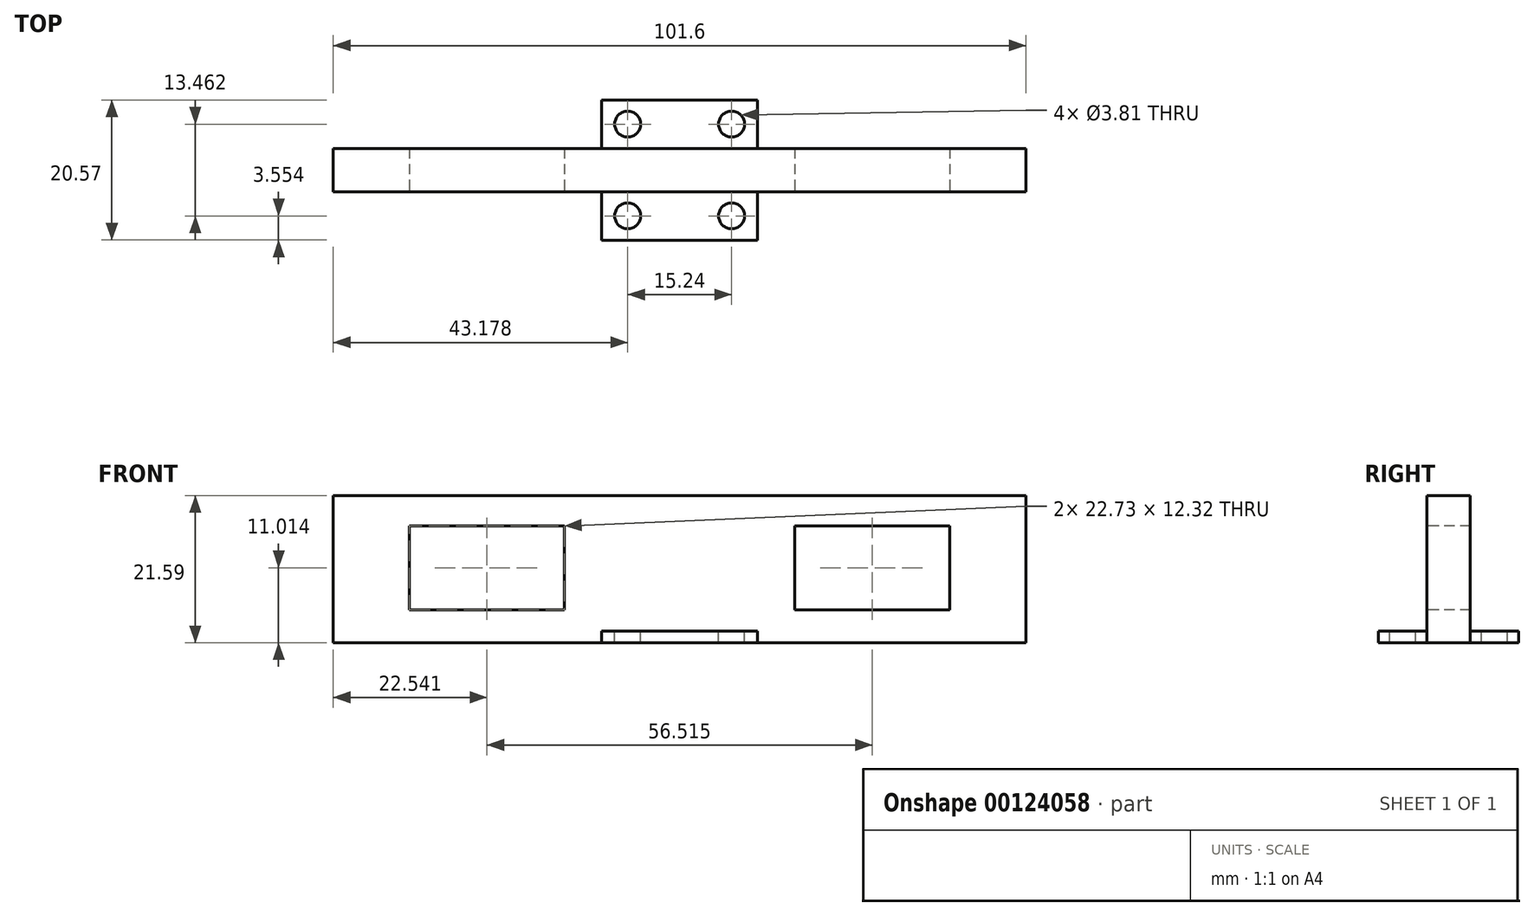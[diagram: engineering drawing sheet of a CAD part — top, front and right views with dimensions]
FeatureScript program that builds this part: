
annotation { "Feature Type Name" : "Feature", "Feature Type Description" : "" }
export const myFeature = defineFeature(function(context is Context, id is Id, definition is map)
    precondition{}
    {
        {
            var Q0;
            Q0=qCreatedBy(makeId("Front.planeOp"),FACE);
            var sketch = newSketch(context, id + "F0", { "sketchPlane" : qUnion([Q0])});
            skLineSegment(sketch, "E0.bottom", {"start": v(-46.15, 32.64) * mm, "end": v(55.45, 32.64) * mm});
            skLineSegment(sketch, "E0.top", {"start": v(-46.15, 11.05) * mm, "end": v(55.45, 11.05) * mm});
            skLineSegment(sketch, "E0.left", {"start": v(-46.15, 32.64) * mm, "end": v(-46.15, 11.05) * mm});
            skLineSegment(sketch, "E0.right", {"start": v(55.45, 32.64) * mm, "end": v(55.45, 11.05) * mm});
            skSolve(sketch);
        }
        {
            var Q0;
            Q0=makeQuery(id+"F0.imprint","IMPRINT",FACE,{"disambiguationData":[TD([[makeQuery(id+"F0.imprint","IMPRINT",EDGE,{"derivedFrom":sQuery(id+"F0.wireOp",EDGE,"E0.bottom")}),-1.0]])]});
            extrude(context, id + "F1", {"entities" : qUnion([Q0]), "depth" : 6.35 * mm});
        }
        {
            var Q0;
            Q0=makeQuery(id+"F1.opExtrude","CAP_FACE",FACE,{"disambiguationData":[OSD([sQuery(id+"F0.wireOp",EDGE,"E0.bottom"),sQuery(id+"F0.wireOp",EDGE,"E0.top"),sQuery(id+"F0.wireOp",EDGE,"E0.left"),sQuery(id+"F0.wireOp",EDGE,"E0.right")])],"isStart":false});
            var sketch = newSketch(context, id + "F2", { "sketchPlane" : qUnion([Q0])});
            skLineSegment(sketch, "E1.bottom", {"start": v(-34.98, 28.22) * mm, "end": v(-12.24, 28.22) * mm});
            skLineSegment(sketch, "E1.top", {"start": v(-34.98, 15.9) * mm, "end": v(-12.24, 15.9) * mm});
            skLineSegment(sketch, "E1.left", {"start": v(-34.98, 28.22) * mm, "end": v(-34.98, 15.9) * mm});
            skLineSegment(sketch, "E1.right", {"start": v(-12.24, 28.22) * mm, "end": v(-12.24, 15.9) * mm});
            skLineSegment(sketch, "E2.bottom", {"start": v(21.54, 28.22) * mm, "end": v(44.27, 28.22) * mm});
            skLineSegment(sketch, "E2.top", {"start": v(21.54, 15.9) * mm, "end": v(44.27, 15.9) * mm});
            skLineSegment(sketch, "E2.left", {"start": v(21.54, 28.22) * mm, "end": v(21.54, 15.9) * mm});
            skLineSegment(sketch, "E2.right", {"start": v(44.27, 28.22) * mm, "end": v(44.27, 15.9) * mm});
            skSolve(sketch);
        }
        {
            var Q0;
            Q0=makeQuery(id+"F2.imprint","IMPRINT",FACE,{"disambiguationData":[TD([[makeQuery(id+"F2.imprint","IMPRINT",EDGE,{"derivedFrom":sQuery(id+"F2.wireOp",EDGE,"E1.bottom")}),-1.0]])]});
            var Q1;
            Q1=makeQuery(id+"F2.imprint","IMPRINT",FACE,{"disambiguationData":[TD([[makeQuery(id+"F2.imprint","IMPRINT",EDGE,{"derivedFrom":sQuery(id+"F2.wireOp",EDGE,"E2.bottom")}),-1.0]])]});
            extrude(context, id + "F3", {"entities" : qUnion([Q0, Q1]), "operationType" : NewBodyOperationType.REMOVE, "oppositeDirection" : true, "depth" : 25.4 * mm});
        }
        {
            var Q0;
            Q0=makeQuery(id+"F1.opExtrude","CAP_FACE",FACE,{"disambiguationData":[OSD([sQuery(id+"F0.wireOp",EDGE,"E0.bottom"),sQuery(id+"F0.wireOp",EDGE,"E0.top"),sQuery(id+"F0.wireOp",EDGE,"E0.left"),sQuery(id+"F0.wireOp",EDGE,"E0.right")])],"isStart":false});
            var sketch = newSketch(context, id + "F4", { "sketchPlane" : qUnion([Q0])});
            skLineSegment(sketch, "E3.bottom", {"start": v(-6.78, 12.76) * mm, "end": v(16.08, 12.76) * mm});
            skLineSegment(sketch, "E3.top", {"start": v(-6.78, 11.05) * mm, "end": v(16.08, 11.05) * mm});
            skLineSegment(sketch, "E3.left", {"start": v(-6.78, 12.76) * mm, "end": v(-6.78, 11.05) * mm});
            skLineSegment(sketch, "E3.right", {"start": v(16.08, 12.76) * mm, "end": v(16.08, 11.05) * mm});
            skSolve(sketch);
        }
        {
            var Q0;
            Q0=makeQuery(id+"F4.imprint","IMPRINT",FACE,{"disambiguationData":[TD([[makeQuery(id+"F4.imprint","IMPRINT",EDGE,{"derivedFrom":sQuery(id+"F4.wireOp",EDGE,"E3.bottom")}),-1.0]])]});
            extrude(context, id + "F5", {"entities" : qUnion([Q0]), "operationType" : NewBodyOperationType.ADD, "depth" : 7.11 * mm});
        }
        {
            var Q0;
            Q0=qCreatedBy(makeId("Front.planeOp"),FACE);
            var sketch = newSketch(context, id + "F6", { "sketchPlane" : qUnion([Q0])});
            skLineSegment(sketch, "E4.bottom", {"start": v(16.08, 12.76) * mm, "end": v(-6.78, 12.76) * mm});
            skLineSegment(sketch, "E4.top", {"start": v(16.08, 11.05) * mm, "end": v(-6.78, 11.05) * mm});
            skLineSegment(sketch, "E4.left", {"start": v(16.08, 12.76) * mm, "end": v(16.08, 11.05) * mm});
            skLineSegment(sketch, "E4.right", {"start": v(-6.78, 12.76) * mm, "end": v(-6.78, 11.05) * mm});
            skSolve(sketch);
        }
        {
            var Q0;
            Q0=makeQuery(id+"F6.imprint","IMPRINT",FACE,{"disambiguationData":[TD([[makeQuery(id+"F6.imprint","IMPRINT",EDGE,{"derivedFrom":sQuery(id+"F6.wireOp",EDGE,"E4.bottom")}),1.0]])]});
            extrude(context, id + "F7", {"entities" : qUnion([Q0]), "operationType" : NewBodyOperationType.ADD, "oppositeDirection" : true, "depth" : 7.11 * mm});
        }
        {
            var Q0;
            Q0=makeQuery(id+"F7.opExtrude","SWEPT_FACE",FACE,{"disambiguationData":[OSD([sQuery(id+"F6.wireOp",EDGE,"E4.bottom")])]});
            var sketch = newSketch(context, id + "F8", { "sketchPlane" : qUnion([Q0])});
            skPoint(sketch, "E5", {"position": v(-2.97, 3.56) * mm});
            skPoint(sketch, "E6", {"position": v(12.27, 3.56) * mm});
            skPoint(sketch, "E7", {"position": v(-2.97, -9.9) * mm});
            skPoint(sketch, "E8", {"position": v(12.27, -9.9) * mm});
            skSolve(sketch);
        }
        {
            var Q0;
            Q0=sQuery(id+"F8.wireOp",VERTEX,"E5");
            var Q1;
            Q1=sQuery(id+"F8.wireOp",VERTEX,"E6");
            var Q2;
            Q2=sQuery(id+"F8.wireOp",VERTEX,"E8");
            var Q3;
            Q3=sQuery(id+"F8.wireOp",VERTEX,"E7");
            var Q4;
            Q4=makeQuery(id+"F1.opExtrude","SWEPT_BODY",BODY,{"disambiguationData":[OSD([sQuery(id+"F0.wireOp",EDGE,"E0.bottom"),sQuery(id+"F0.wireOp",EDGE,"E0.top"),sQuery(id+"F0.wireOp",EDGE,"E0.left"),sQuery(id+"F0.wireOp",EDGE,"E0.right")])]});
            hole(context, id + "F9", {"style" : HoleStyle.SIMPLE, "endStyle" : HoleEndStyle.THROUGH, "holeDiameter" : 3.8 * mm, "locations" : qUnion([Q0, Q1, Q2, Q3]), "scope" : qUnion([Q4]), "isTappedThrough" : true});
        }
    });
